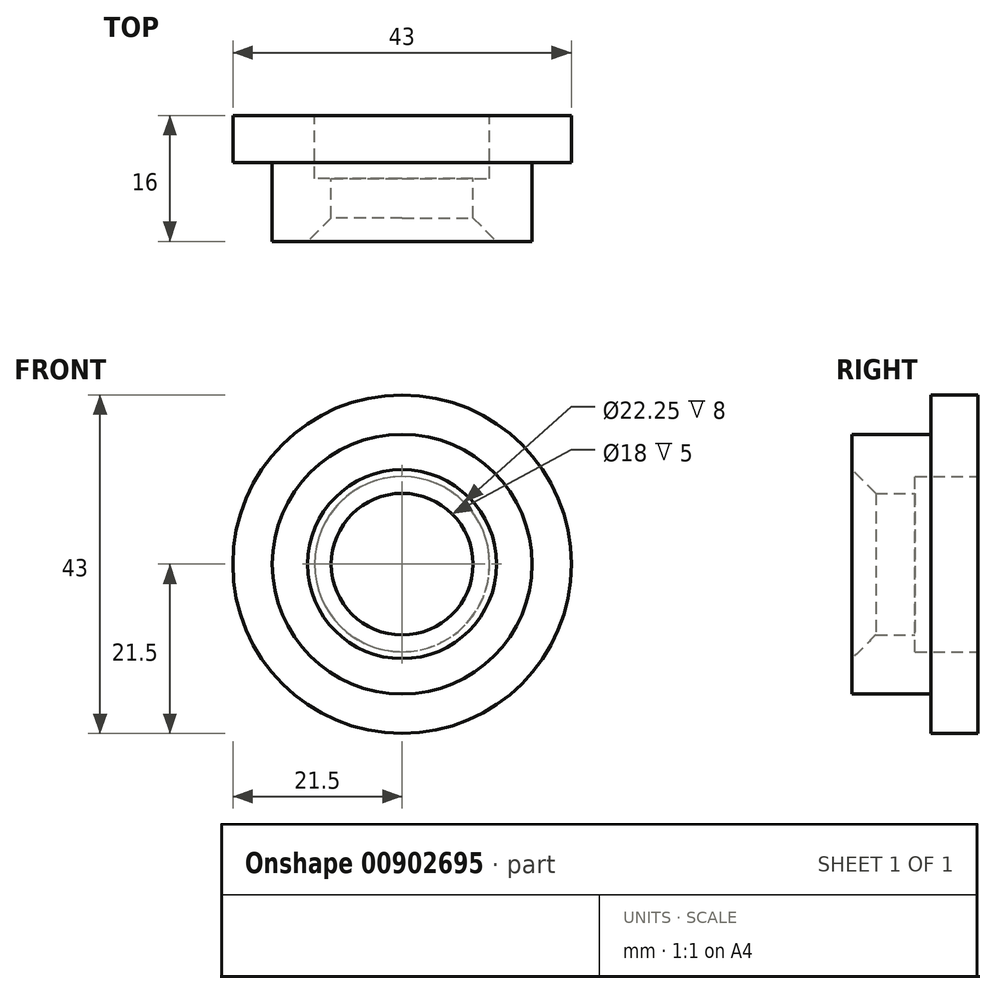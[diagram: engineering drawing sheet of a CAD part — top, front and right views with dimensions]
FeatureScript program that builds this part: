
annotation { "Feature Type Name" : "Feature", "Feature Type Description" : "" }
export const myFeature = defineFeature(function(context is Context, id is Id, definition is map)
    precondition{}
    {
        {
            var Q0;
            Q0=qCreatedBy(makeId("Front.planeOp"),FACE);
            var sketch = newSketch(context, id + "F0", { "sketchPlane" : qUnion([Q0])});
            skCircle(sketch, "E0", {"center": v(0, 0) * mm, "radius": 21.5 * mm});
            skSolve(sketch);
        }
        {
            var Q0;
            Q0 = qSketchRegion(id + "F0", true);
            extrude(context, id + "F1", {"entities" : qUnion([Q0]), "oppositeDirection" : true, "depth" : 6 * mm, "offsetDistance" : 25 * mm});
        }
        {
            var Q0;
            Q0=makeQuery(id+"F1.opExtrude","CAP_FACE",FACE,{"disambiguationData":[OSD([sQuery(id+"F0.wireOp",EDGE,"E0")])],"isStart":true});
            var sketch = newSketch(context, id + "F2", { "sketchPlane" : qUnion([Q0])});
            skCircle(sketch, "E1", {"center": v(0, 0) * mm, "radius": 16.5 * mm});
            skSolve(sketch);
        }
        {
            var Q0;
            Q0 = qSketchRegion(id + "F2", true);
            extrude(context, id + "F3", {"entities" : qUnion([Q0]), "operationType" : NewBodyOperationType.ADD, "depth" : 10 * mm, "offsetDistance" : 25 * mm});
        }
        {
            var Q0;
            Q0=makeQuery(id+"F1.opExtrude","CAP_FACE",FACE,{"disambiguationData":[OSD([sQuery(id+"F0.wireOp",EDGE,"E0")])],"isStart":false});
            var sketch = newSketch(context, id + "F4", { "sketchPlane" : qUnion([Q0])});
            skCircle(sketch, "E2", {"center": v(0, 0) * mm, "radius": 11.13 * mm});
            skSolve(sketch);
        }
        {
            var Q0;
            Q0=makeQuery(id+"F4.imprint","IMPRINT",FACE,{"disambiguationData":[TD([[makeQuery(id+"F4.imprint","IMPRINT",EDGE,{"derivedFrom":sQuery(id+"F4.wireOp",EDGE,"E2")}),1.0]])]});
            var Q1;
            Q1=makeQuery(id+"F3.opExtrude","CAP_FACE",FACE,{"disambiguationData":[OSD([sQuery(id+"F2.wireOp",EDGE,"E1")])],"isStart":false});
            extrude(context, id + "F5", {"entities" : qUnion([Q0]), "operationType" : NewBodyOperationType.REMOVE, "endBound" : BoundingType.UP_TO_SURFACE, "oppositeDirection" : true, "depth" : 8.5 * mm, "endBoundEntityFace" : qUnion([Q1]), "hasOffset" : true, "offsetDistance" : 8 * mm});
        }
        {
            var Q0;
            Q0=makeQuery(id+"F5.boolean.opBoolean","COPY",FACE,{"derivedFrom":makeQuery(id+"F5.opExtrude","CAP_FACE",FACE,{"disambiguationData":[OSD([sQuery(id+"F4.wireOp",EDGE,"E2")])],"isStart":false})});
            var sketch = newSketch(context, id + "F6", { "sketchPlane" : qUnion([Q0])});
            skCircle(sketch, "E3", {"center": v(0, 0) * mm, "radius": 9 * mm});
            skSolve(sketch);
        }
        {
            var Q0;
            Q0=qSketchRegion(id+"F6",true);
            var Q1;
            Q1=makeQuery(id+"F3.opExtrude","CAP_FACE",FACE,{"disambiguationData":[OSD([sQuery(id+"F2.wireOp",EDGE,"E1"),sQuery(id+"F2.wireOp",EDGE,"61a21257-e9d0-42e5-b150-992a49e10002")])],"isStart":false});
            extrude(context, id + "F7", {"entities" : qUnion([Q0]), "operationType" : NewBodyOperationType.REMOVE, "endBound" : BoundingType.THROUGH_ALL, "oppositeDirection" : true, "depth" : 5 * mm, "endBoundEntityFace" : qUnion([Q1]), "offsetDistance" : 7 * mm});
        }
        {
            var Q0;
            Q0=makeQuery(id+"F7.boolean.opBoolean","INTERSECT",EDGE,{"derivedFrom":[makeQuery(id+"F3.opExtrude","CAP_FACE",FACE,{"disambiguationData":[OSD([sQuery(id+"F2.wireOp",EDGE,"E1")])],"isStart":false}),makeQuery(id+"F7.opExtrude","SWEPT_FACE",FACE,{"disambiguationData":[OSD([sQuery(id+"F6.wireOp",EDGE,"E3")])]})]});
            chamfer(context, id + "F8", {"entities" : qUnion([Q0]), "width" : 3 * mm, "tangentPropagation" : true});
        }
    });
